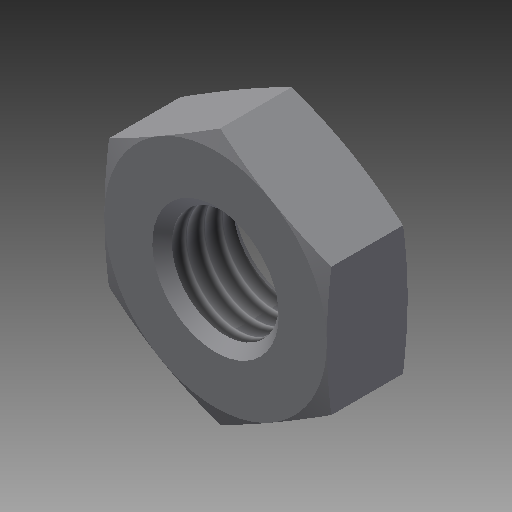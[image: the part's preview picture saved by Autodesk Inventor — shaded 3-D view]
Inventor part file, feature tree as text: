
AUTODESK INVENTOR PART (.ipt)
format: ipt  version: 2019 (Build 230136000, 136)  size: 178,688 bytes
history: native  units: in
note: dims shown in document units (in); Inventor stores cm internally (conversion verified against a paired STEP export)
features: other x70, sketch x3, revolve x2, extrude x1, thread x1
ambient origin geometry x8: Origin, YZ Plane, XZ Plane, XY Plane, X Axis, Y Axis, Z Axis, Center Point
bodies: Solid1 (feature_tree)
feature tree (77):
  sketch  "Sketch_8"  dims[d0=360.0deg d1=0.16in d2=0.0in]
  sketch  "Sketch_10"  dims[d3=360.0deg d4=0.1213in d5=0.0in]
  revolve  "Revolution1"  [1 undecoded]
  extrude  "Extrusion1"  Depth=0.1213in TaperAngle=0.0deg
  revolve  "Revolution2"  [1 undecoded]
  thread  "Thread1"  [1 undecoded]
  other  "NUT_XY"
  other  "NUT_YZ"
  other  "NUT_ZX"
  other  "NUT_X"
  other  "NUT_Y"
  other  "NUT_Z"
  other  "NUT_Center"
  other  "a1_XY"
  other  "a1_YZ"
  other  "a1_ZX"
  other  "a1_X"
  other  "a1_Y"
  other  "a1_Z"
  other  "a1_Center"
  other  "a2_XY"
  other  "a2_YZ"
  other  "a2_ZX"
  other  "a2_X"
  other  "a2_Y"
  other  "a2_Z"
  other  "a2_Center"
  other  "b1_XY"
  other  "b1_YZ"
  other  "b1_ZX"
  other  "b1_X"
  other  "b1_Y"
  other  "b1_Z"
  other  "b1_Center"
  other  "b2_XY"
  other  "b2_YZ"
  other  "b2_ZX"
  other  "b2_X"
  other  "b2_Y"
  other  "b2_Z"
  other  "b2_Center"
  other  "e_XY"
  other  "e_YZ"
  other  "e_ZX"
  other  "e_X"
  other  "e_Y"
  other  "e_Z"
  other  "e_Center"
  other  "ol1_XY"
  other  "ol1_YZ"
  other  "ol1_ZX"
  other  "ol1_X"
  other  "ol1_Y"
  other  "ol1_Z"
  other  "ol1_Center"
  other  "ol2_XY"
  other  "ol2_YZ"
  other  "ol2_ZX"
  other  "ol2_X"
  other  "ol2_Y"
  other  "ol2_Z"
  other  "ol2_Center"
  other  "th1_XY"
  other  "th1_YZ"
  other  "th1_ZX"
  other  "th1_X"
  other  "th1_Y"
  other  "th1_Z"
  other  "th1_Center"
  other  "th2_XY"
  other  "th2_YZ"
  other  "th2_ZX"
  other  "th2_X"
  other  "th2_Y"
  other  "th2_Z"
  other  "th2_Center"
  sketch  "Sketch_11"  dims[d6=0.0in d7=0.0in d8=0.0in]
note: 3 required parameter values undecoded (feature->parameter linkage not recoverable at this tier; creation-order binding heuristic only, values carry confidence <= 0.55)